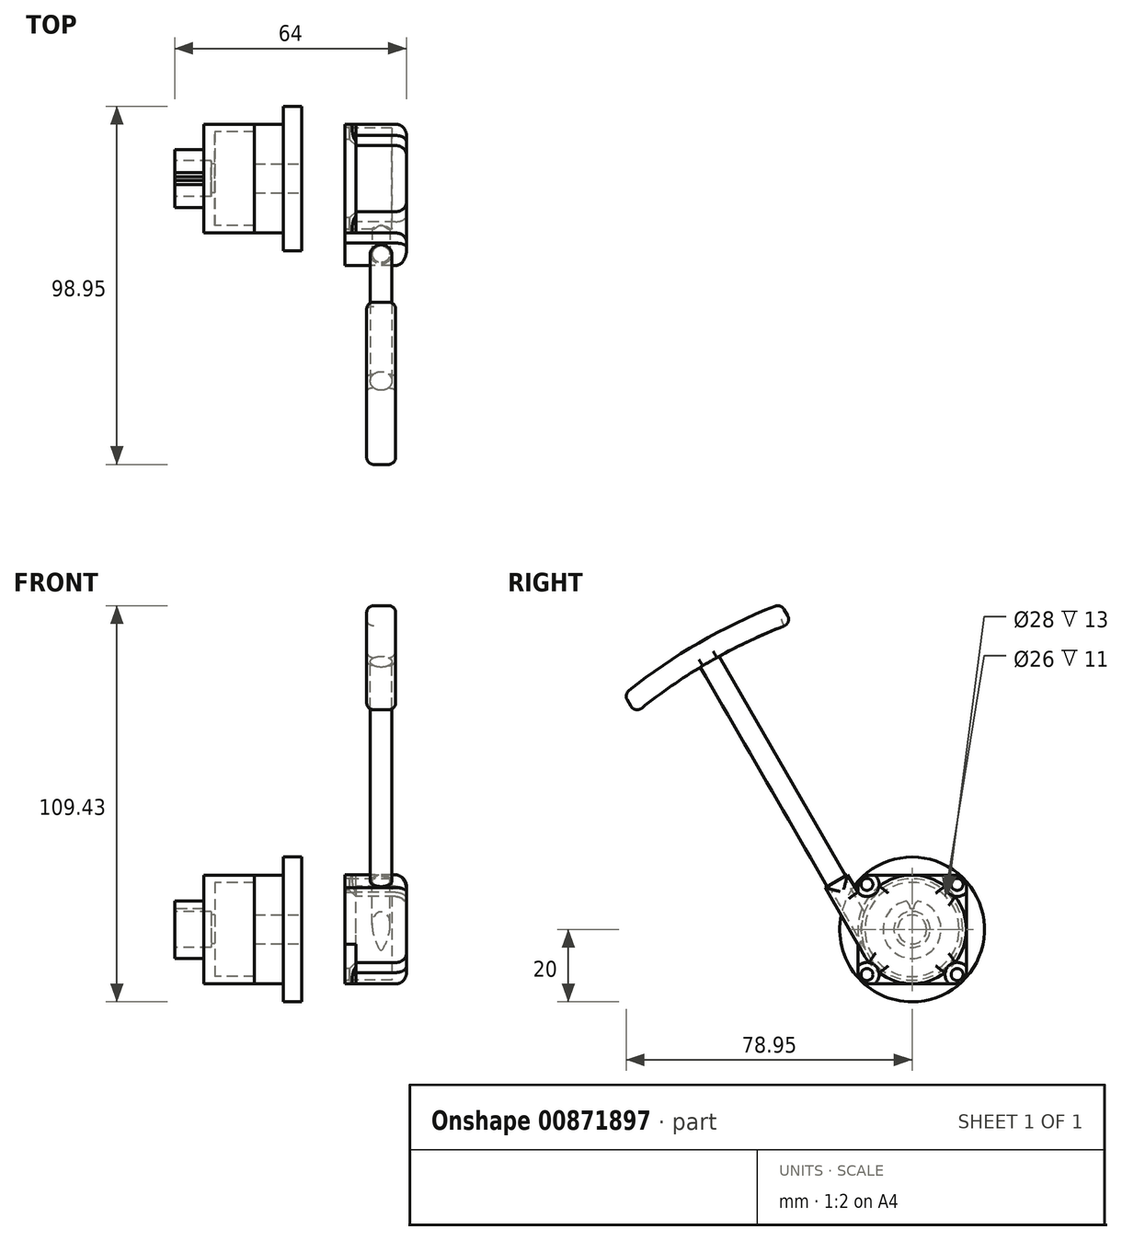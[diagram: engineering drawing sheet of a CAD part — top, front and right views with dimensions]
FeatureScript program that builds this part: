
annotation { "Feature Type Name" : "Feature", "Feature Type Description" : "" }
export const myFeature = defineFeature(function(context is Context, id is Id, definition is map)
    precondition{}
    {
        {
            var Q0;
            Q0=qCreatedBy(makeId("Front.planeOp"),FACE);
            var sketch = newSketch(context, id + "F0", { "sketchPlane" : qUnion([Q0])});
            skLineSegment(sketch, "E0.bottom", {"start": v(0, 15) * mm, "end": v(-14, 15) * mm});
            skLineSegment(sketch, "E0.left", {"start": v(0, 15) * mm, "end": v(0, 0) * mm});
            skLineSegment(sketch, "E0.right", {"start": v(-14, 15) * mm, "end": v(-14, 8) * mm});
            skLineSegment(sketch, "E1", {"start": v(-14, 8) * mm, "end": v(-22, 8) * mm});
            skLineSegment(sketch, "E2", {"start": v(-22, 8) * mm, "end": v(-22, 0) * mm});
            skLineSegment(sketch, "E3", {"start": v(-22, 0) * mm, "end": v(0, 0) * mm});
            skPoint(sketch, "E4.orphan", {"position": v(-22, -8) * mm});
            skLineSegment(sketch, "E5", {"start": v(-35.57, 0) * mm, "end": v(5.94, 0) * mm, "construction": true});
            skSolve(sketch);
        }
        {
            var Q0;
            Q0=makeQuery(id+"F0.imprint","IMPRINT",FACE,{"disambiguationData":[TD([[makeQuery(id+"F0.imprint","IMPRINT",EDGE,{"derivedFrom":sQuery(id+"F0.wireOp",EDGE,"E0.bottom")}),1.0]])]});
            var Q1;
            Q1=sQuery(id+"F0.wireOp",EDGE,"E5");
            revolve(context, id + "F1", {"surfaceOperationType" : NewSurfaceOperationType.NEW, "entities" : qUnion([Q0]), "axis" : qUnion([Q1]), "revolveType" : RevolveType.FULL});
        }
        {
            var Q0;
            Q0=makeQuery(id+"F1.opRevolve","SWEPT_FACE",FACE,{"disambiguationData":[OSD([sQuery(id+"F0.wireOp",EDGE,"E2")])]});
            var sketch = newSketch(context, id + "F2", { "sketchPlane" : qUnion([Q0])});
            skLineSegment(sketch, "E6", {"start": v(0, 0) * mm, "end": v(0, 9.53) * mm, "construction": true});
            skArc(sketch, "E7", {"start": v(0.5, 5.73) * mm, "mid": v(0, 5.75) * mm, "end": v(-0.5, 5.73) * mm});
            skFitSpline(sketch, "E8", {"points": [v(-0.5, 5.73) * mm, v(-1.6, 7.84) * mm], "startDerivative": vector(0, 1.56) * mm, "endDerivative": vector(-2.08, 1.3) * mm});
            skArc(sketch, "E9.0", {"start": v(1.6, 7.84) * mm, "mid": v(0, 8) * mm, "end": v(-1.6, 7.84) * mm});
            skFitSpline(sketch, "E10.MirrorCS", {"points": [v(0.5, 5.73) * mm, v(1.6, 7.84) * mm], "startDerivative": vector(0, 1.56) * mm, "endDerivative": vector(2.08, 1.3) * mm});
            skLineSegment(sketch, "E11", {"start": v(-0.5, 5.73) * mm, "end": v(-0.5, 4.57) * mm, "construction": true});
            skSolve(sketch);
        }
        {
            var Q0;
            Q0=qSketchRegion(id+"F2",true);
            var Q1;
            Q1=makeQuery(id+"F1.opRevolve","SWEPT_FACE",FACE,{"disambiguationData":[OSD([sQuery(id+"F0.wireOp",EDGE,"E0.right")])]});
            extrude(context, id + "F3", {"entities" : qUnion([Q0]), "operationType" : NewBodyOperationType.REMOVE, "endBound" : BoundingType.UP_TO_SURFACE, "oppositeDirection" : true, "depth" : 25 * mm, "endBoundEntityFace" : qUnion([Q1]), "offsetDistance" : 25 * mm});
        }
        {
            var Q0;
            Q0=qCreatedBy(makeId("Front.planeOp"),FACE);
            var sketch = newSketch(context, id + "F4", { "sketchPlane" : qUnion([Q0])});
            skLineSegment(sketch, "E12.bottom", {"start": v(0, 0) * mm, "end": v(-22, 0) * mm});
            skLineSegment(sketch, "E12.top", {"start": v(0, 13) * mm, "end": v(-11, 13) * mm});
            skLineSegment(sketch, "E12.left", {"start": v(0, 0) * mm, "end": v(0, 13) * mm});
            skLineSegment(sketch, "E12.right", {"start": v(-11, 0) * mm, "end": v(-11, 13) * mm});
            skLineSegment(sketch, "E13", {"start": v(-14, 15) * mm, "end": v(0, 15) * mm, "construction": true});
            skLineSegment(sketch, "E14.0", {"start": v(-14, -15) * mm, "end": v(-14, 15) * mm, "construction": true});
            skLineSegment(sketch, "E15", {"start": v(-12, 5) * mm, "end": v(-22, 5) * mm});
            skLineSegment(sketch, "E16", {"start": v(-22, 5) * mm, "end": v(-22, 0) * mm});
            skLineSegment(sketch, "E17", {"start": v(-11, 4) * mm, "end": v(-12, 4) * mm});
            skLineSegment(sketch, "E18", {"start": v(-12, 4) * mm, "end": v(-12, 5) * mm});
            skLineSegment(sketch, "E19", {"start": v(0, 0) * mm, "end": v(3.87, 0) * mm, "construction": true});
            skSolve(sketch);
        }
        {
            var Q0;
            Q0=qSketchRegion(id+"F4",true);
            var Q1;
            Q1=sQuery(id+"F4.wireOp",EDGE,"E19");
            revolve(context, id + "F5", {"operationType" : NewBodyOperationType.REMOVE, "surfaceOperationType" : NewSurfaceOperationType.NEW, "entities" : qUnion([Q0]), "axis" : qUnion([Q1]), "revolveType" : RevolveType.FULL});
        }
        {
            var Q0;
            Q0=makeQuery(id+"F1.opRevolve","SWEPT_FACE",FACE,{"disambiguationData":[OSD([sQuery(id+"F0.wireOp",EDGE,"E0.left")])]});
            var sketch = newSketch(context, id + "F6", { "sketchPlane" : qUnion([Q0])});
            skCircle(sketch, "E20.0", {"center": v(0, 0) * mm, "radius": 15 * mm});
            skSolve(sketch);
        }
        {
            var Q0;
            Q0=qSketchRegion(id+"F6",true);
            extrude(context, id + "F7", {"entities" : qUnion([Q0]), "depth" : 8 * mm, "offsetDistance" : 25 * mm});
        }
        {
            var Q0;
            Q0=makeQuery(id+"F7.opExtrude","CAP_FACE",FACE,{"disambiguationData":[OSD([sQuery(id+"F6.wireOp",EDGE,"E20.0")])],"isStart":false});
            var sketch = newSketch(context, id + "F8", { "sketchPlane" : qUnion([Q0])});
            skCircle(sketch, "E21", {"center": v(0, 0) * mm, "radius": 20 * mm});
            skSolve(sketch);
        }
        {
            var Q0;
            Q0=qSketchRegion(id+"F8",true);
            extrude(context, id + "F9", {"entities" : qUnion([Q0]), "operationType" : NewBodyOperationType.ADD, "depth" : 5 * mm, "offsetDistance" : 25 * mm});
        }
        {
            var Q0;
            Q0=makeQuery(id+"F9.opExtrude","CAP_FACE",FACE,{"disambiguationData":[OSD([sQuery(id+"F8.wireOp",EDGE,"E21")])],"isStart":false});
            var sketch = newSketch(context, id + "F10", { "sketchPlane" : qUnion([Q0])});
            skCircle(sketch, "E22", {"center": v(0, 0) * mm, "radius": 4 * mm});
            skSolve(sketch);
        }
        {
            var Q0;
            Q0=qSketchRegion(id+"F10",true);
            extrude(context, id + "F11", {"entities" : qUnion([Q0]), "operationType" : NewBodyOperationType.REMOVE, "oppositeDirection" : true, "depth" : 25 * mm, "offsetDistance" : 25 * mm});
        }
        {
            var Q0;
            Q0=qCreatedBy(makeId("Right.planeOp"),FACE);
            cPlane(context, id + "F12", {"entities" : qUnion([Q0]), "cplaneType" : CPlaneType.OFFSET, "offset" : 25 * mm, "width" : 150 * mm, "height" : 150 * mm});
        }
        {
            var Q0;
            Q0=qCreatedBy(id+"F12.planeOp",FACE);
            var sketch = newSketch(context, id + "F13", { "sketchPlane" : qUnion([Q0])});
            skLineSegment(sketch, "E23.bottom", {"start": v(15, -15) * mm, "end": v(-15, -15) * mm});
            skLineSegment(sketch, "E23.top", {"start": v(15, 15) * mm, "end": v(-15, 15) * mm});
            skLineSegment(sketch, "E23.left", {"start": v(15, -15) * mm, "end": v(15, 15) * mm});
            skLineSegment(sketch, "E23.right", {"start": v(-15, -15) * mm, "end": v(-15, 15) * mm});
            skPoint(sketch, "E23.middle", {"position": v(0, 0) * mm});
            skLineSegment(sketch, "E24.bottom", {"start": v(12.45, 12.45) * mm, "end": v(-12.45, 12.45) * mm, "construction": true});
            skLineSegment(sketch, "E24.top", {"start": v(12.45, -12.45) * mm, "end": v(-12.45, -12.45) * mm, "construction": true});
            skLineSegment(sketch, "E24.left", {"start": v(12.45, 12.45) * mm, "end": v(12.45, -12.45) * mm, "construction": true});
            skLineSegment(sketch, "E24.right", {"start": v(-12.45, 12.45) * mm, "end": v(-12.45, -12.45) * mm, "construction": true});
            skSolve(sketch);
        }
        {
            var Q0;
            Q0=qSketchRegion(id+"F13",true);
            extrude(context, id + "F14", {"entities" : qUnion([Q0]), "depth" : 3 * mm, "offsetDistance" : 25 * mm});
        }
        {
            var Q0;
            {var subQ0=sQuery(id+"F13.wireOp",EDGE,"E23.left");var subQ1=sQuery(id+"F13.wireOp",EDGE,"E23.top");var subQ2=makeQuery(id+"F14.opExtrude","CAP_FACE",FACE,{"disambiguationData":[OSD([sQuery(id+"F13.wireOp",EDGE,"E23.bottom"),subQ1,subQ0,sQuery(id+"F13.wireOp",EDGE,"E23.right")])],"isStart":false});Q0=makeQuery(id+"F18.boolean.opBoolean","SPLIT",FACE,{"disambiguationData":[TD([subQ2,makeQuery(id+"F14.opExtrude","SWEPT_FACE",FACE,{"disambiguationData":[OSD([subQ1])]}),makeQuery(id+"F14.opExtrude","SWEPT_FACE",FACE,{"disambiguationData":[OSD([subQ0])]}),makeQuery(id+"F18.opExtrude","SWEPT_FACE",FACE,{"disambiguationData":[OSD([sQuery(id+"F17.wireOp",EDGE,"E29")])]})])],"derivedFrom":subQ2});}
            var sketch = newSketch(context, id + "F15", { "sketchPlane" : qUnion([Q0])});
            skPoint(sketch, "E25.0", {"position": v(-12.45, 12.45) * mm});
            skPoint(sketch, "E26.0", {"position": v(12.45, 12.45) * mm});
            skPoint(sketch, "E27.0", {"position": v(12.45, -12.45) * mm});
            skPoint(sketch, "E28.0", {"position": v(-12.45, -12.45) * mm});
            skSolve(sketch);
        }
        {
            var Q0;
            Q0=sQuery(id+"F15.wireOp",VERTEX,"E26.0");
            var Q1;
            Q1=sQuery(id+"F15.wireOp",VERTEX,"E27.0");
            var Q2;
            Q2=sQuery(id+"F15.wireOp",VERTEX,"E28.0");
            var Q3;
            Q3=sQuery(id+"F15.wireOp",VERTEX,"E25.0");
            var Q4;
            Q4=makeQuery(id+"F14.opExtrude","SWEPT_BODY",BODY,{"disambiguationData":[OSD([sQuery(id+"F13.wireOp",EDGE,"E23.bottom"),sQuery(id+"F13.wireOp",EDGE,"E23.top"),sQuery(id+"F13.wireOp",EDGE,"E23.left"),sQuery(id+"F13.wireOp",EDGE,"E23.right")])]});
            hole(context, id + "F16", {"style" : HoleStyle.C_SINK, "endStyle" : HoleEndStyle.BLIND, "standardTappedOrClearance" : lookupTablePath({ "fit" : "Normal", "standard" : "ISO", "size" : "M3", "type" : "Clearance" }), "standardBlindInLast" : lookupTablePath({ "fit" : "Standard", "standard" : "ISO", "size" : "M3", "type" : "Clearance" }), "holeDiameter" : 3.3 * mm, "cSinkDiameter" : 6.72 * mm, "cSinkAngle" : 90 * degree, "majorDiameter" : 5 * mm, "holeDepth" : 14.1 * mm, "isTappedThrough" : true, "tappedDepth" : 12 * mm, "tapClearance" : 3, "locations" : qUnion([Q0, Q1, Q2, Q3]), "scope" : qUnion([Q4])});
        }
        {
            var Q0;
            Q0=makeQuery(id+"F14.opExtrude","CAP_FACE",FACE,{"disambiguationData":[OSD([sQuery(id+"F13.wireOp",EDGE,"E23.bottom"),sQuery(id+"F13.wireOp",EDGE,"E23.top"),sQuery(id+"F13.wireOp",EDGE,"E23.left"),sQuery(id+"F13.wireOp",EDGE,"E23.right")])],"isStart":false});
            var sketch = newSketch(context, id + "F17", { "sketchPlane" : qUnion([Q0])});
            skArc(sketch, "E29", {"start": v(-13, -7.5) * mm, "mid": v(-12.47, -8.34) * mm, "end": v(-11.9, -9.14) * mm});
            skLineSegment(sketch, "E30", {"start": v(0, 0) * mm, "end": v(-19.04, 32.98) * mm, "construction": true});
            skLineSegment(sketch, "E31", {"start": v(0, 0) * mm, "end": v(0, 29.7) * mm, "construction": true});
            skLineSegment(sketch, "E32", {"start": v(-24, 11.55) * mm, "end": v(-13, -7.5) * mm});
            skArc(sketch, "E33.0", {"start": v(9.14, 11.9) * mm, "mid": v(10.07, 10.07) * mm, "end": v(11.9, 9.14) * mm});
            skArc(sketch, "E34.0", {"start": v(11.9, -9.14) * mm, "mid": v(10.07, -10.07) * mm, "end": v(9.14, -11.9) * mm});
            skArc(sketch, "E35.0", {"start": v(-9.14, -11.9) * mm, "mid": v(-10.07, -10.07) * mm, "end": v(-11.9, -9.14) * mm});
            skArc(sketch, "E36.trimOffspring", {"start": v(-9.14, -11.9) * mm, "mid": v(0, -15) * mm, "end": v(9.14, -11.9) * mm});
            skArc(sketch, "E37.trimOffspring", {"start": v(11.9, -9.14) * mm, "mid": v(15, 0) * mm, "end": v(11.9, 9.14) * mm});
            skArc(sketch, "E38.trimOffspring", {"start": v(9.14, 11.9) * mm, "mid": v(0, 15) * mm, "end": v(-9.14, 11.9) * mm});
            skArc(sketch, "E39.0", {"start": v(-15, 10.26) * mm, "mid": v(-10.07, 10.07) * mm, "end": v(-10.26, 15) * mm});
            skLineSegment(sketch, "E40", {"start": v(-15, 10.26) * mm, "end": v(-17.8, 15.12) * mm});
            skLineSegment(sketch, "E41", {"start": v(-17.8, 15.12) * mm, "end": v(-24, 11.55) * mm});
            skSolve(sketch);
        }
        {
            var Q0;
            Q0=qSketchRegion(id+"F17",true);
            extrude(context, id + "F18", {"entities" : qUnion([Q0]), "operationType" : NewBodyOperationType.ADD, "depth" : 14 * mm, "offsetDistance" : 25 * mm});
        }
        {
            var Q0;
            Q0=makeQuery(id+"F18.opExtrude","CAP_FACE",FACE,{"disambiguationData":[OSD([sQuery(id+"F17.wireOp",EDGE,"E29"),sQuery(id+"F17.wireOp",EDGE,"E32"),sQuery(id+"F17.wireOp",EDGE,"E33.0"),sQuery(id+"F17.wireOp",EDGE,"E34.0"),sQuery(id+"F17.wireOp",EDGE,"E35.0"),sQuery(id+"F17.wireOp",EDGE,"E36.trimOffspring"),sQuery(id+"F17.wireOp",EDGE,"E37.trimOffspring"),sQuery(id+"F17.wireOp",EDGE,"E38.trimOffspring"),sQuery(id+"F17.wireOp",EDGE,"E39.0"),sQuery(id+"F17.wireOp",EDGE,"E40"),sQuery(id+"F17.wireOp",EDGE,"E41")])],"isStart":true});
            var Q1;
            Q1=makeQuery(id+"F18.opExtrude","CAP_FACE",FACE,{"disambiguationData":[OSD([sQuery(id+"F17.wireOp",EDGE,"E29"),sQuery(id+"F17.wireOp",EDGE,"E32"),sQuery(id+"F17.wireOp",EDGE,"E33.0"),sQuery(id+"F17.wireOp",EDGE,"E34.0"),sQuery(id+"F17.wireOp",EDGE,"E35.0"),sQuery(id+"F17.wireOp",EDGE,"E36.trimOffspring"),sQuery(id+"F17.wireOp",EDGE,"E37.trimOffspring"),sQuery(id+"F17.wireOp",EDGE,"E38.trimOffspring"),sQuery(id+"F17.wireOp",EDGE,"E39.0"),sQuery(id+"F17.wireOp",EDGE,"E40"),sQuery(id+"F17.wireOp",EDGE,"E41")])],"isStart":false});
            cPlane(context, id + "F19", {"entities" : qUnion([Q0, Q1]), "cplaneType" : CPlaneType.MID_PLANE, "offset" : 25 * mm, "width" : 150 * mm, "height" : 150 * mm});
        }
        {
            var Q0;
            Q0=qCreatedBy(id+"F19.planeOp",FACE);
            var sketch = newSketch(context, id + "F20", { "sketchPlane" : qUnion([Q0])});
            skLineSegment(sketch, "E42.0", {"start": v(17.8, 15.12) * mm, "end": v(24, 11.55) * mm, "construction": true});
            skLineSegment(sketch, "E43", {"start": v(20.9, 13.34) * mm, "end": v(17.36, 7.21) * mm, "construction": true});
            skLineSegment(sketch, "E44", {"start": v(20.9, 13.34) * mm, "end": v(23.5, 11.84) * mm});
            skLineSegment(sketch, "E45", {"start": v(23.5, 11.84) * mm, "end": v(58.5, 72.46) * mm});
            skLineSegment(sketch, "E46", {"start": v(58.5, 72.46) * mm, "end": v(55.9, 73.96) * mm});
            skLineSegment(sketch, "E47", {"start": v(55.9, 73.96) * mm, "end": v(20.9, 13.34) * mm});
            skSolve(sketch);
        }
        {
            var Q0;
            Q0=qSketchRegion(id+"F20",true);
            var Q1;
            Q1=sQuery(id+"F20.wireOp",EDGE,"E43");
            revolve(context, id + "F21", {"surfaceOperationType" : NewSurfaceOperationType.NEW, "entities" : qUnion([Q0]), "axis" : qUnion([Q1]), "revolveType" : RevolveType.FULL});
        }
        {
            var Q0;
            Q0=qCreatedBy(id+"F19.planeOp",FACE);
            var sketch = newSketch(context, id + "F22", { "sketchPlane" : qUnion([Q0])});
            skLineSegment(sketch, "E48.0", {"start": v(53.3, 75.46) * mm, "end": v(58.5, 72.46) * mm, "construction": true});
            skLineSegment(sketch, "E49", {"start": v(55.9, 73.96) * mm, "end": v(46.13, 57.05) * mm, "construction": true});
            skArc(sketch, "E50", {"start": v(76.5, 59.64) * mm, "mid": v(55.9, 73.96) * mm, "end": v(33.2, 84.64) * mm});
            skLineSegment(sketch, "E51", {"start": v(76.5, 59.64) * mm, "end": v(79.54, 64.9) * mm});
            skLineSegment(sketch, "E52", {"start": v(36.24, 89.9) * mm, "end": v(33.2, 84.64) * mm});
            skArc(sketch, "E53.0", {"start": v(79.54, 64.9) * mm, "mid": v(58.9, 79.16) * mm, "end": v(36.24, 89.9) * mm});
            skSolve(sketch);
        }
        {
            var Q0;
            Q0=makeQuery(id+"F22.imprint","IMPRINT",FACE,{"disambiguationData":[TD([[makeQuery(id+"F22.imprint","IMPRINT",EDGE,{"derivedFrom":sQuery(id+"F22.wireOp",EDGE,"E50")}),-1.0]])]});
            var Q1;
            Q1=sQuery(id+"F22.wireOp",EDGE,"E53.0");
            extrude(context, id + "F23", {"entities" : qUnion([Q0]), "operationType" : NewBodyOperationType.ADD, "surfaceEntities" : qUnion([Q1]), "depth" : 8 * mm, "offsetDistance" : 25 * mm, "symmetric" : true});
        }
        {
            var Q0;
            Q0=makeQuery(id+"F23.opExtrude","SWEPT_FACE",FACE,{"disambiguationData":[OSD([sQuery(id+"F22.wireOp",EDGE,"E53.0")])]});
            var Q1;
            Q1=makeQuery(id+"F23.opExtrude","CAP_EDGE",EDGE,{"disambiguationData":[OSD([sQuery(id+"F22.wireOp",EDGE,"E50")])],"isStart":true});
            var Q2;
            Q2=makeQuery(id+"F23.opExtrude","CAP_EDGE",EDGE,{"disambiguationData":[OSD([sQuery(id+"F22.wireOp",EDGE,"E50")])],"isStart":false});
            var Q3;
            Q3=makeQuery(id+"F23.opExtrude","SWEPT_FACE",FACE,{"disambiguationData":[OSD([sQuery(id+"F22.wireOp",EDGE,"E52")])]});
            var Q4;
            Q4=makeQuery(id+"F23.opExtrude","SWEPT_FACE",FACE,{"disambiguationData":[OSD([sQuery(id+"F22.wireOp",EDGE,"E51")])]});
            fillet(context, id + "F24", {"entities" : qUnion([Q0, Q1, Q2, Q3, Q4]), "radius" : 2 * mm, "tangentPropagation" : true, "allowEdgeOverflow" : false});
        }
        {
            var Q0;
            Q0=makeQuery(id+"F18.opExtrude","CAP_FACE",FACE,{"disambiguationData":[OSD([sQuery(id+"F17.wireOp",EDGE,"E29"),sQuery(id+"F17.wireOp",EDGE,"E32"),sQuery(id+"F17.wireOp",EDGE,"E33.0"),sQuery(id+"F17.wireOp",EDGE,"E34.0"),sQuery(id+"F17.wireOp",EDGE,"E35.0"),sQuery(id+"F17.wireOp",EDGE,"E36.trimOffspring"),sQuery(id+"F17.wireOp",EDGE,"E37.trimOffspring"),sQuery(id+"F17.wireOp",EDGE,"E38.trimOffspring"),sQuery(id+"F17.wireOp",EDGE,"E39.0"),sQuery(id+"F17.wireOp",EDGE,"E40"),sQuery(id+"F17.wireOp",EDGE,"E41")])],"isStart":false});
            var Q1;
            Q1=makeQuery(id+"F14.opExtrude","SWEPT_EDGE",EDGE,{"disambiguationData":[OSD([sQuery(id+"F13.wireOp",EDGE,"E23.bottom"),sQuery(id+"F13.wireOp",EDGE,"E23.left")])]});
            var Q2;
            Q2=makeQuery(id+"F14.opExtrude","SWEPT_EDGE",EDGE,{"disambiguationData":[OSD([sQuery(id+"F13.wireOp",EDGE,"E23.bottom"),sQuery(id+"F13.wireOp",EDGE,"E23.right")])]});
            var Q3;
            Q3=makeQuery(id+"F14.opExtrude","SWEPT_EDGE",EDGE,{"disambiguationData":[OSD([sQuery(id+"F13.wireOp",EDGE,"E23.top"),sQuery(id+"F13.wireOp",EDGE,"E23.left")])]});
            var Q4;
            Q4=makeQuery(id+"F14.opExtrude","SWEPT_EDGE",EDGE,{"disambiguationData":[OSD([sQuery(id+"F13.wireOp",EDGE,"E23.top"),sQuery(id+"F13.wireOp",EDGE,"E23.right")])]});
            fillet(context, id + "F25", {"entities" : qUnion([Q0, Q1, Q2, Q3, Q4]), "radius" : 3 * mm, "tangentPropagation" : true, "allowEdgeOverflow" : false});
        }
        {
            var Q0;
            Q0=makeQuery(id+"F18.opExtrude","CAP_FACE",FACE,{"disambiguationData":[OSD([sQuery(id+"F17.wireOp",EDGE,"E29"),sQuery(id+"F17.wireOp",EDGE,"E32"),sQuery(id+"F17.wireOp",EDGE,"E33.0"),sQuery(id+"F17.wireOp",EDGE,"E34.0"),sQuery(id+"F17.wireOp",EDGE,"E35.0"),sQuery(id+"F17.wireOp",EDGE,"E36.trimOffspring"),sQuery(id+"F17.wireOp",EDGE,"E37.trimOffspring"),sQuery(id+"F17.wireOp",EDGE,"E38.trimOffspring"),sQuery(id+"F17.wireOp",EDGE,"E39.0"),sQuery(id+"F17.wireOp",EDGE,"E40"),sQuery(id+"F17.wireOp",EDGE,"E41")])],"isStart":true});
            var Q1;
            Q1=makeQuery(id+"F14.opExtrude","CAP_FACE",FACE,{"disambiguationData":[OSD([sQuery(id+"F13.wireOp",EDGE,"E23.bottom"),sQuery(id+"F13.wireOp",EDGE,"E23.top"),sQuery(id+"F13.wireOp",EDGE,"E23.left"),sQuery(id+"F13.wireOp",EDGE,"E23.right")])],"isStart":true});
            extrude(context, id + "F26", {"entities" : qUnion([Q0]), "operationType" : NewBodyOperationType.ADD, "endBound" : BoundingType.UP_TO_SURFACE, "depth" : 25 * mm, "endBoundEntityFace" : qUnion([Q1]), "offsetDistance" : 25 * mm});
        }
        {
            var Q0;
            {var subQ0=sQuery(id+"F13.wireOp",EDGE,"E23.right");var subQ1=sQuery(id+"F13.wireOp",EDGE,"E23.left");var subQ2=sQuery(id+"F13.wireOp",EDGE,"E23.top");var subQ3=sQuery(id+"F13.wireOp",EDGE,"E23.bottom");Q0=makeQuery(id+"F26.boolean.opBoolean","MERGE",FACE,{"derivedFrom":[makeQuery(id+"F14.opExtrude","CAP_FACE",FACE,{"disambiguationData":[OSD([subQ3,subQ2,subQ1,subQ0])],"isStart":true}),makeQuery(id+"F26.opExtrude","CAP_FACE",FACE,{"disambiguationData":[OSD([subQ3,subQ2,subQ1,subQ0])],"isStart":false})]});}
            var sketch = newSketch(context, id + "F27", { "sketchPlane" : qUnion([Q0])});
            skPoint(sketch, "E54.0", {"position": v(0, 0) * mm});
            skCircle(sketch, "E55", {"center": v(0, 0) * mm, "radius": 14 * mm});
            skSolve(sketch);
        }
        {
            var Q0;
            Q0=qSketchRegion(id+"F27",true);
            extrude(context, id + "F28", {"entities" : qUnion([Q0]), "operationType" : NewBodyOperationType.REMOVE, "oppositeDirection" : true, "depth" : 13 * mm, "offsetDistance" : 25 * mm});
        }
        {
            var Q0;
            {var subQ0=sQuery(id+"F17.wireOp",EDGE,"E41");Q0=makeQuery(id+"F26.boolean.opBoolean","MERGE",FACE,{"derivedFrom":[makeQuery(id+"F18.opExtrude","SWEPT_FACE",FACE,{"disambiguationData":[OSD([subQ0])]}),makeQuery(id+"F26.opExtrude","SWEPT_FACE",FACE,{"disambiguationData":[OSD([subQ0])]})]});}
            var sketch = newSketch(context, id + "F29", { "sketchPlane" : qUnion([Q0])});
            skCircle(sketch, "E56", {"center": v(35, -11.43) * mm, "radius": 2.5 * mm});
            skLineSegment(sketch, "E57", {"start": v(25, -11.43) * mm, "end": v(35, -11.43) * mm, "construction": true});
            skSolve(sketch);
        }
        {
            var Q0;
            Q0=makeQuery(id+"F29.imprint","IMPRINT",FACE,{"disambiguationData":[TD([[makeQuery(id+"F29.imprint","IMPRINT",EDGE,{"derivedFrom":sQuery(id+"F29.wireOp",EDGE,"E56")}),1.0]])]});
            extrude(context, id + "F30", {"entities" : qUnion([Q0]), "operationType" : NewBodyOperationType.REMOVE, "oppositeDirection" : true, "depth" : 22 * mm, "offsetDistance" : 25 * mm});
        }
    });
